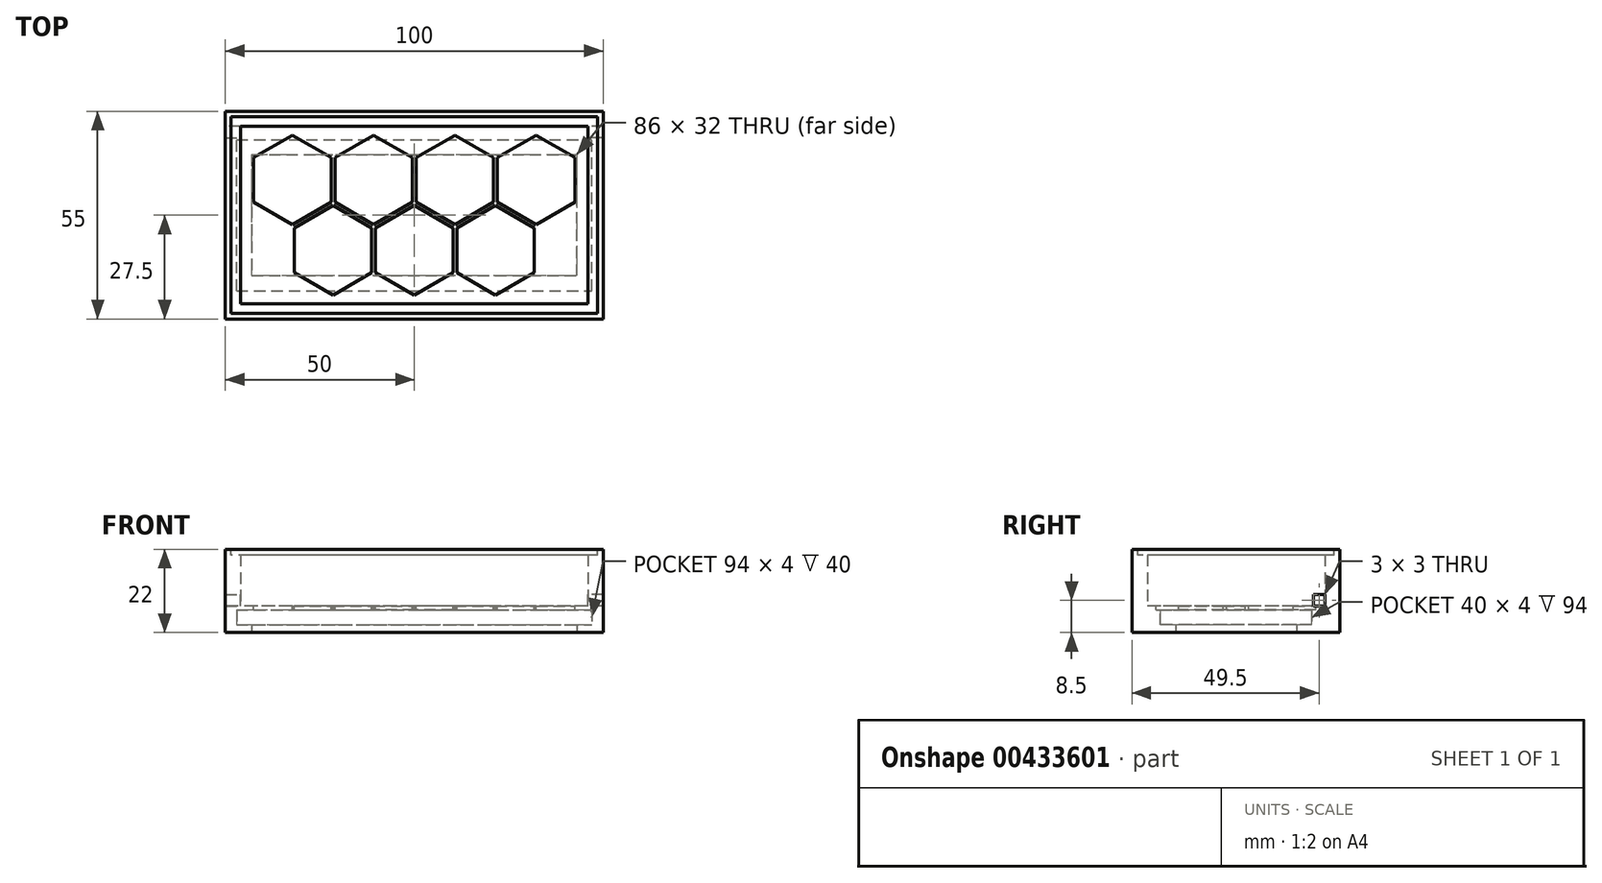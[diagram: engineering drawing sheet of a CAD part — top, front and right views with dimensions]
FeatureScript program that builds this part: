
annotation { "Feature Type Name" : "Feature", "Feature Type Description" : "" }
export const myFeature = defineFeature(function(context is Context, id is Id, definition is map)
    precondition{}
    {
        {
            var Q0;
            Q0=qCreatedBy(makeId("Top.planeOp"),FACE);
            var sketch = newSketch(context, id + "F0", { "sketchPlane" : qUnion([Q0])});
            skLineSegment(sketch, "E0.bottom", {"start": v(50, 27.5) * mm, "end": v(-50, 27.5) * mm});
            skLineSegment(sketch, "E0.top", {"start": v(50, -27.5) * mm, "end": v(-50, -27.5) * mm});
            skLineSegment(sketch, "E0.left", {"start": v(50, 27.5) * mm, "end": v(50, -27.5) * mm});
            skLineSegment(sketch, "E0.right", {"start": v(-50, 27.5) * mm, "end": v(-50, -27.5) * mm});
            skPoint(sketch, "E0.middle", {"position": v(0, 0) * mm});
            skSolve(sketch);
        }
        {
            var Q0;
            Q0=makeQuery(id+"F0.imprint","IMPRINT",FACE,{"disambiguationData":[TD([[makeQuery(id+"F0.imprint","IMPRINT",EDGE,{"derivedFrom":sQuery(id+"F0.wireOp",EDGE,"E0.bottom")}),1.0]])]});
            var Q1;
            Q1=qNothing();
            extrude(context, id + "F1", {"entities" : qUnion([Q0]), "surfaceEntities" : qUnion([Q1]), "depth" : 7 * mm});
        }
        {
            var Q0;
            Q0=makeQuery(id+"F1.opExtrude","CAP_FACE",FACE,{"disambiguationData":[OSD([sQuery(id+"F0.wireOp",EDGE,"E0.bottom"),sQuery(id+"F0.wireOp",EDGE,"E0.top"),sQuery(id+"F0.wireOp",EDGE,"E0.left"),sQuery(id+"F0.wireOp",EDGE,"E0.right")])],"isStart":false});
            var sketch = newSketch(context, id + "F2", { "sketchPlane" : qUnion([Q0])});
            skLineSegment(sketch, "E1.bottom", {"start": v(46, 23.5) * mm, "end": v(-46, 23.5) * mm});
            skLineSegment(sketch, "E1.top", {"start": v(46, -23.5) * mm, "end": v(-46, -23.5) * mm});
            skLineSegment(sketch, "E1.left", {"start": v(46, 23.5) * mm, "end": v(46, -23.5) * mm});
            skLineSegment(sketch, "E1.right", {"start": v(-46, 23.5) * mm, "end": v(-46, -23.5) * mm});
            skPoint(sketch, "E1.middle", {"position": v(0, 0) * mm});
            skSolve(sketch);
        }
        {
            var Q0;
            Q0=makeQuery(id+"F2.imprint","IMPRINT",FACE,{"disambiguationData":[TD([[makeQuery(id+"F2.imprint","IMPRINT",EDGE,{"derivedFrom":sQuery(id+"F2.wireOp",EDGE,"E1.bottom")}),-1.0]])]});
            extrude(context, id + "F3", {"entities" : qUnion([Q0]), "operationType" : NewBodyOperationType.ADD, "depth" : 15 * mm});
        }
        {
            var Q0;
            Q0=makeQuery(id+"F3.opExtrude","CAP_FACE",FACE,{"disambiguationData":[OSD([sQuery(id+"F0.wireOp",EDGE,"E0.bottom"),sQuery(id+"F0.wireOp",EDGE,"E0.top"),sQuery(id+"F0.wireOp",EDGE,"E0.left"),sQuery(id+"F0.wireOp",EDGE,"E0.right"),sQuery(id+"F2.wireOp",EDGE,"E1.bottom"),sQuery(id+"F2.wireOp",EDGE,"E1.top"),sQuery(id+"F2.wireOp",EDGE,"E1.left"),sQuery(id+"F2.wireOp",EDGE,"E1.right")])],"isStart":false});
            var sketch = newSketch(context, id + "F4", { "sketchPlane" : qUnion([Q0])});
            skLineSegment(sketch, "E2.bottom", {"start": v(48.5, 26) * mm, "end": v(-48.5, 26) * mm});
            skLineSegment(sketch, "E2.top", {"start": v(48.5, -26) * mm, "end": v(-48.5, -26) * mm});
            skLineSegment(sketch, "E2.left", {"start": v(48.5, 26) * mm, "end": v(48.5, -26) * mm});
            skLineSegment(sketch, "E2.right", {"start": v(-48.5, 26) * mm, "end": v(-48.5, -26) * mm});
            skSolve(sketch);
        }
        {
            var Q0;
            Q0=makeQuery(id+"F4.imprint","IMPRINT",FACE,{"disambiguationData":[TD([[makeQuery(id+"F4.imprint","IMPRINT",EDGE,{"derivedFrom":sQuery(id+"F4.wireOp",EDGE,"E2.bottom")}),1.0]])]});
            extrude(context, id + "F5", {"entities" : qUnion([Q0]), "operationType" : NewBodyOperationType.REMOVE, "oppositeDirection" : true, "depth" : 1.5 * mm});
        }
        {
            var Q0;
            Q0=makeQuery(id+"F1.opExtrude","CAP_FACE",FACE,{"disambiguationData":[OSD([sQuery(id+"F0.wireOp",EDGE,"E0.bottom"),sQuery(id+"F0.wireOp",EDGE,"E0.top"),sQuery(id+"F0.wireOp",EDGE,"E0.left"),sQuery(id+"F0.wireOp",EDGE,"E0.right")])],"isStart":false});
            var sketch = newSketch(context, id + "F6", { "sketchPlane" : qUnion([Q0])});
            skLineSegment(sketch, "E3", {"start": v(0, -23.5) * mm, "end": v(0, -21.15) * mm});
            skPoint(sketch, "E3.endSnap0", {"position": v(0, -23.5) * mm});
            skCircle(sketch, "E4.cCircle", {"center": v(0, -9.31) * mm, "radius": 11.84 * mm, "construction": true});
            skLineSegment(sketch, "E4.0", {"start": v(0, -21.15) * mm, "end": v(-10.25, -15.23) * mm});
            skLineSegment(sketch, "E4.1", {"start": v(-10.25, -15.23) * mm, "end": v(-10.25, -3.4) * mm});
            skLineSegment(sketch, "E4.2", {"start": v(-10.25, -3.4) * mm, "end": v(0, 2.52) * mm});
            skLineSegment(sketch, "E4.3", {"start": v(0, 2.52) * mm, "end": v(10.25, -3.4) * mm});
            skLineSegment(sketch, "E4.4", {"start": v(10.25, -3.4) * mm, "end": v(10.25, -15.23) * mm});
            skLineSegment(sketch, "E4.5", {"start": v(10.25, -15.23) * mm, "end": v(0, -21.15) * mm});
            skCircle(sketch, "E5.cCircle", {"center": v(-21.5, -9.31) * mm, "radius": 10.25 * mm, "construction": true});
            skLineSegment(sketch, "E5.0", {"start": v(-11.25, -3.4) * mm, "end": v(-11.25, -15.23) * mm});
            skLineSegment(sketch, "E5.1", {"start": v(-11.25, -15.23) * mm, "end": v(-21.5, -21.15) * mm});
            skLineSegment(sketch, "E5.2", {"start": v(-21.5, -21.15) * mm, "end": v(-31.75, -15.23) * mm});
            skLineSegment(sketch, "E5.3", {"start": v(-31.75, -15.23) * mm, "end": v(-31.75, -3.4) * mm});
            skLineSegment(sketch, "E5.4", {"start": v(-31.75, -3.4) * mm, "end": v(-21.5, 2.52) * mm});
            skLineSegment(sketch, "E5.5", {"start": v(-21.5, 2.52) * mm, "end": v(-11.25, -3.4) * mm});
            skPoint(sketch, "E5.0.midPoint", {"position": v(-11.25, -9.31) * mm});
            skCircle(sketch, "E6.cCircle", {"center": v(21.5, -9.31) * mm, "radius": 10.25 * mm, "construction": true});
            skLineSegment(sketch, "E6.0", {"start": v(31.75, -3.4) * mm, "end": v(31.75, -15.23) * mm});
            skLineSegment(sketch, "E6.1", {"start": v(31.75, -15.23) * mm, "end": v(21.5, -21.15) * mm});
            skLineSegment(sketch, "E6.2", {"start": v(21.5, -21.15) * mm, "end": v(11.25, -15.23) * mm});
            skLineSegment(sketch, "E6.3", {"start": v(11.25, -15.23) * mm, "end": v(11.25, -3.4) * mm});
            skLineSegment(sketch, "E6.4", {"start": v(11.25, -3.4) * mm, "end": v(21.5, 2.52) * mm});
            skLineSegment(sketch, "E6.5", {"start": v(21.5, 2.52) * mm, "end": v(31.75, -3.4) * mm});
            skPoint(sketch, "E6.0.midPoint", {"position": v(31.75, -9.31) * mm});
            skCircle(sketch, "E7.cCircle", {"center": v(-32.25, 9.3) * mm, "radius": 10.25 * mm, "construction": true});
            skLineSegment(sketch, "E7.0", {"start": v(-22, 15.23) * mm, "end": v(-22, 3.4) * mm});
            skLineSegment(sketch, "E7.1", {"start": v(-22, 3.4) * mm, "end": v(-32.25, -2.53) * mm});
            skLineSegment(sketch, "E7.2", {"start": v(-32.25, -2.53) * mm, "end": v(-42.5, 3.4) * mm});
            skLineSegment(sketch, "E7.3", {"start": v(-42.5, 3.4) * mm, "end": v(-42.5, 15.23) * mm});
            skLineSegment(sketch, "E7.4", {"start": v(-42.5, 15.23) * mm, "end": v(-32.25, 21.15) * mm});
            skLineSegment(sketch, "E7.5", {"start": v(-32.25, 21.15) * mm, "end": v(-22, 15.23) * mm});
            skPoint(sketch, "E7.0.midPoint", {"position": v(-22, 9.3) * mm});
            skCircle(sketch, "E8.cCircle", {"center": v(-10.75, 9.3) * mm, "radius": 10.25 * mm, "construction": true});
            skLineSegment(sketch, "E8.0", {"start": v(-0.5, 15.23) * mm, "end": v(-0.5, 3.39) * mm});
            skLineSegment(sketch, "E8.1", {"start": v(-0.5, 3.39) * mm, "end": v(-10.75, -2.53) * mm});
            skLineSegment(sketch, "E8.2", {"start": v(-10.75, -2.53) * mm, "end": v(-21, 3.39) * mm});
            skLineSegment(sketch, "E8.3", {"start": v(-21, 3.39) * mm, "end": v(-21, 15.23) * mm});
            skLineSegment(sketch, "E8.4", {"start": v(-21, 15.23) * mm, "end": v(-10.75, 21.15) * mm});
            skLineSegment(sketch, "E8.5", {"start": v(-10.75, 21.15) * mm, "end": v(-0.5, 15.23) * mm});
            skPoint(sketch, "E8.0.midPoint", {"position": v(-0.5, 9.3) * mm});
            skCircle(sketch, "E9.cCircle", {"center": v(10.75, 9.3) * mm, "radius": 10.25 * mm, "construction": true});
            skLineSegment(sketch, "E9.0", {"start": v(21, 15.23) * mm, "end": v(21, 3.39) * mm});
            skLineSegment(sketch, "E9.1", {"start": v(21, 3.39) * mm, "end": v(10.75, -2.53) * mm});
            skLineSegment(sketch, "E9.2", {"start": v(10.75, -2.53) * mm, "end": v(0.5, 3.39) * mm});
            skLineSegment(sketch, "E9.3", {"start": v(0.5, 3.39) * mm, "end": v(0.5, 15.23) * mm});
            skLineSegment(sketch, "E9.4", {"start": v(0.5, 15.23) * mm, "end": v(10.75, 21.14) * mm});
            skLineSegment(sketch, "E9.5", {"start": v(10.75, 21.14) * mm, "end": v(21, 15.23) * mm});
            skPoint(sketch, "E9.0.midPoint", {"position": v(21, 9.3) * mm});
            skCircle(sketch, "E10.cCircle", {"center": v(32.25, 9.3) * mm, "radius": 10.25 * mm, "construction": true});
            skLineSegment(sketch, "E10.0", {"start": v(42.5, 15.23) * mm, "end": v(42.5, 3.39) * mm});
            skLineSegment(sketch, "E10.1", {"start": v(42.5, 3.39) * mm, "end": v(32.25, -2.53) * mm});
            skLineSegment(sketch, "E10.2", {"start": v(32.25, -2.53) * mm, "end": v(22, 3.39) * mm});
            skLineSegment(sketch, "E10.3", {"start": v(22, 3.39) * mm, "end": v(22, 15.23) * mm});
            skLineSegment(sketch, "E10.4", {"start": v(22, 15.23) * mm, "end": v(32.25, 21.14) * mm});
            skLineSegment(sketch, "E10.5", {"start": v(32.25, 21.14) * mm, "end": v(42.5, 15.23) * mm});
            skPoint(sketch, "E10.0.midPoint", {"position": v(42.5, 9.3) * mm});
            skSolve(sketch);
        }
        {
            var Q0;
            Q0=makeQuery(id+"F3.opExtrude","SWEPT_FACE",FACE,{"disambiguationData":[OSD([sQuery(id+"F2.wireOp",EDGE,"E1.left")])]});
            var sketch = newSketch(context, id + "F7", { "sketchPlane" : qUnion([Q0])});
            skLineSegment(sketch, "E11.bottom", {"start": v(-23.5, 7) * mm, "end": v(-20.5, 7) * mm});
            skLineSegment(sketch, "E11.top", {"start": v(-23.5, 10) * mm, "end": v(-20.5, 10) * mm});
            skLineSegment(sketch, "E11.left", {"start": v(-23.5, 7) * mm, "end": v(-23.5, 10) * mm});
            skLineSegment(sketch, "E11.right", {"start": v(-20.5, 7) * mm, "end": v(-20.5, 10) * mm});
            skSolve(sketch);
        }
        {
            var Q0;
            Q0=makeQuery(id+"F7.imprint","IMPRINT",FACE,{"disambiguationData":[TD([[makeQuery(id+"F7.imprint","IMPRINT",EDGE,{"derivedFrom":sQuery(id+"F7.wireOp",EDGE,"E11.bottom")}),1.0]])]});
            extrude(context, id + "F8", {"entities" : qUnion([Q0]), "operationType" : NewBodyOperationType.REMOVE, "oppositeDirection" : true, "depth" : 5 * mm});
        }
        {
            var Q0;
            Q0=makeQuery(id+"F3.opExtrude","SWEPT_FACE",FACE,{"disambiguationData":[OSD([sQuery(id+"F2.wireOp",EDGE,"E1.right")])]});
            var sketch = newSketch(context, id + "F9", { "sketchPlane" : qUnion([Q0])});
            skLineSegment(sketch, "E12.bottom", {"start": v(23.5, 7) * mm, "end": v(20.5, 7) * mm});
            skLineSegment(sketch, "E12.top", {"start": v(23.5, 10) * mm, "end": v(20.5, 10) * mm});
            skLineSegment(sketch, "E12.left", {"start": v(23.5, 7) * mm, "end": v(23.5, 10) * mm});
            skLineSegment(sketch, "E12.right", {"start": v(20.5, 7) * mm, "end": v(20.5, 10) * mm});
            skSolve(sketch);
        }
        {
            var Q0;
            Q0=makeQuery(id+"F9.imprint","IMPRINT",FACE,{"disambiguationData":[TD([[makeQuery(id+"F9.imprint","IMPRINT",EDGE,{"derivedFrom":sQuery(id+"F9.wireOp",EDGE,"E12.bottom")}),-1.0]])]});
            extrude(context, id + "F10", {"entities" : qUnion([Q0]), "operationType" : NewBodyOperationType.REMOVE, "oppositeDirection" : true, "depth" : 5 * mm});
        }
        {
            var Q0;
            {var subQ0=sQuery(id+"F0.wireOp",EDGE,"E0.left");Q0=makeQuery(id+"F3.boolean.opBoolean","MERGE",FACE,{"derivedFrom":[makeQuery(id+"F1.opExtrude","SWEPT_FACE",FACE,{"disambiguationData":[OSD([subQ0])]}),makeQuery(id+"F3.opExtrude","SWEPT_FACE",FACE,{"disambiguationData":[OSD([subQ0])]})]});}
            var sketch = newSketch(context, id + "F11", { "sketchPlane" : qUnion([Q0])});
            skLineSegment(sketch, "E13", {"start": v(-20, 0) * mm, "end": v(-20, 6) * mm});
            skLineSegment(sketch, "E14", {"start": v(-20, 6) * mm, "end": v(20, 6) * mm});
            skLineSegment(sketch, "E15", {"start": v(20, 6) * mm, "end": v(20, 0) * mm});
            skSolve(sketch);
        }
        {
            var Q0;
            {var subQ0=sQuery(id+"F11.wireOp",EDGE,"E13");Q0=makeQuery(id+"F11.imprint","IMPRINT",FACE,{"disambiguationData":[TD([[makeQuery(id+"F11.imprint","IMPRINT",EDGE,{"derivedFrom":subQ0}),-1.0]])]});}
            extrude(context, id + "F12", {"entities" : qUnion([Q0]), "operationType" : NewBodyOperationType.REMOVE, "oppositeDirection" : true, "depth" : 100 * mm});
        }
        {
            var Q0;
            {var subQ0=sQuery(id+"F0.wireOp",EDGE,"E0.left");Q0=makeQuery(id+"F3.boolean.opBoolean","MERGE",FACE,{"derivedFrom":[makeQuery(id+"F1.opExtrude","SWEPT_FACE",FACE,{"disambiguationData":[OSD([subQ0])]}),makeQuery(id+"F3.opExtrude","SWEPT_FACE",FACE,{"disambiguationData":[OSD([subQ0])]})]});}
            var sketch = newSketch(context, id + "F13", { "sketchPlane" : qUnion([Q0])});
            skLineSegment(sketch, "E16", {"start": v(-16, 2) * mm, "end": v(-20, 2) * mm});
            skLineSegment(sketch, "E17", {"start": v(16, 2) * mm, "end": v(20, 2) * mm});
            skLineSegment(sketch, "E18", {"start": v(16, 2) * mm, "end": v(16, 0) * mm});
            skLineSegment(sketch, "E19", {"start": v(16, 0) * mm, "end": v(20, 0) * mm});
            skLineSegment(sketch, "E20", {"start": v(-16, 2) * mm, "end": v(-16, 0) * mm});
            skLineSegment(sketch, "E21", {"start": v(-16, 0) * mm, "end": v(-20, 0) * mm});
            skSolve(sketch);
        }
        {
            var Q0;
            {var subQ0=sQuery(id+"F13.wireOp",EDGE,"E17");Q0=makeQuery(id+"F13.imprint","IMPRINT",FACE,{"disambiguationData":[TD([[makeQuery(id+"F13.imprint","IMPRINT",EDGE,{"derivedFrom":subQ0}),-1.0]])]});}
            var Q1;
            {var subQ0=sQuery(id+"F13.wireOp",EDGE,"E16");Q1=makeQuery(id+"F13.imprint","IMPRINT",FACE,{"disambiguationData":[TD([[makeQuery(id+"F13.imprint","IMPRINT",EDGE,{"derivedFrom":subQ0}),1.0]])]});}
            extrude(context, id + "F14", {"entities" : qUnion([Q0, Q1]), "operationType" : NewBodyOperationType.ADD, "oppositeDirection" : true, "depth" : 100 * mm});
        }
        {
            var Q0;
            {var subQ0=sQuery(id+"F0.wireOp",EDGE,"E0.left");Q0=makeQuery(id+"F14.boolean.opBoolean","MERGE",FACE,{"derivedFrom":[makeQuery(id+"F3.boolean.opBoolean","MERGE",FACE,{"derivedFrom":[makeQuery(id+"F1.opExtrude","SWEPT_FACE",FACE,{"disambiguationData":[OSD([subQ0])]}),makeQuery(id+"F3.opExtrude","SWEPT_FACE",FACE,{"disambiguationData":[OSD([subQ0])]})]}),makeQuery(id+"F14.opExtrude","CAP_FACE",FACE,{"disambiguationData":[OSD([sQuery(id+"F11.wireOp",EDGE,"E13"),sQuery(id+"F13.wireOp",EDGE,"E16"),sQuery(id+"F13.wireOp",EDGE,"E20"),sQuery(id+"F13.wireOp",EDGE,"E21")])],"isStart":true}),makeQuery(id+"F14.opExtrude","CAP_FACE",FACE,{"disambiguationData":[OSD([sQuery(id+"F11.wireOp",EDGE,"E15"),sQuery(id+"F13.wireOp",EDGE,"E17"),sQuery(id+"F13.wireOp",EDGE,"E18"),sQuery(id+"F13.wireOp",EDGE,"E19")])],"isStart":true})]});}
            var sketch = newSketch(context, id + "F15", { "sketchPlane" : qUnion([Q0])});
            skLineSegment(sketch, "E22", {"start": v(-16, 0) * mm, "end": v(16, 0) * mm});
            skSolve(sketch);
        }
        {
            var Q0;
            Q0=makeQuery(id+"F15.imprint","IMPRINT",FACE,{"disambiguationData":[TD([[makeQuery(id+"F15.imprint","IMPRINT",EDGE,{"derivedFrom":sQuery(id+"F15.wireOp",EDGE,"E22")}),1.0]])]});
            extrude(context, id + "F16", {"entities" : qUnion([Q0]), "operationType" : NewBodyOperationType.ADD, "oppositeDirection" : true, "depth" : 7 * mm});
        }
        {
            var Q0;
            {var subQ0=sQuery(id+"F0.wireOp",EDGE,"E0.right");Q0=makeQuery(id+"F14.boolean.opBoolean","MERGE",FACE,{"derivedFrom":[makeQuery(id+"F3.boolean.opBoolean","MERGE",FACE,{"derivedFrom":[makeQuery(id+"F1.opExtrude","SWEPT_FACE",FACE,{"disambiguationData":[OSD([subQ0])]}),makeQuery(id+"F3.opExtrude","SWEPT_FACE",FACE,{"disambiguationData":[OSD([subQ0])]})]}),makeQuery(id+"F14.opExtrude","CAP_FACE",FACE,{"disambiguationData":[OSD([sQuery(id+"F11.wireOp",EDGE,"E13"),sQuery(id+"F13.wireOp",EDGE,"E16"),sQuery(id+"F13.wireOp",EDGE,"E20"),sQuery(id+"F13.wireOp",EDGE,"E21")])],"isStart":false}),makeQuery(id+"F14.opExtrude","CAP_FACE",FACE,{"disambiguationData":[OSD([sQuery(id+"F11.wireOp",EDGE,"E15"),sQuery(id+"F13.wireOp",EDGE,"E17"),sQuery(id+"F13.wireOp",EDGE,"E18"),sQuery(id+"F13.wireOp",EDGE,"E19")])],"isStart":false})]});}
            var sketch = newSketch(context, id + "F17", { "sketchPlane" : qUnion([Q0])});
            skLineSegment(sketch, "E23", {"start": v(-16, 0) * mm, "end": v(16, 0) * mm});
            skSolve(sketch);
        }
        {
            var Q0;
            Q0=makeQuery(id+"F17.imprint","IMPRINT",FACE,{"disambiguationData":[TD([[makeQuery(id+"F17.imprint","IMPRINT",EDGE,{"derivedFrom":sQuery(id+"F17.wireOp",EDGE,"E23")}),1.0]])]});
            extrude(context, id + "F18", {"entities" : qUnion([Q0]), "operationType" : NewBodyOperationType.ADD, "oppositeDirection" : true, "depth" : 7 * mm});
        }
        {
            var Q0;
            Q0=makeQuery(id+"F16.opExtrude","CAP_FACE",FACE,{"disambiguationData":[OSD([sQuery(id+"F11.wireOp",EDGE,"E13"),sQuery(id+"F11.wireOp",EDGE,"E14"),sQuery(id+"F11.wireOp",EDGE,"E15"),sQuery(id+"F13.wireOp",EDGE,"E16"),sQuery(id+"F13.wireOp",EDGE,"E17"),sQuery(id+"F13.wireOp",EDGE,"E18"),sQuery(id+"F13.wireOp",EDGE,"E20"),sQuery(id+"F15.wireOp",EDGE,"E22")])],"isStart":false});
            var sketch = newSketch(context, id + "F19", { "sketchPlane" : qUnion([Q0])});
            skLineSegment(sketch, "E24", {"start": v(16, 2) * mm, "end": v(-16, 2) * mm});
            skSolve(sketch);
        }
        {
            var Q0;
            Q0 = qSketchRegion(id + "F19", true);
            var Q1;
            Q1=makeQuery(id+"F19.imprint","IMPRINT",FACE,{"disambiguationData":[TD([[makeQuery(id+"F19.imprint","IMPRINT",EDGE,{"derivedFrom":sQuery(id+"F19.wireOp",EDGE,"E24")}),-1.0]])]});
            extrude(context, id + "F20", {"entities" : qUnion([Q0, Q1]), "operationType" : NewBodyOperationType.REMOVE, "oppositeDirection" : true, "depth" : 4 * mm});
        }
        {
            var Q0;
            Q0=makeQuery(id+"F18.opExtrude","CAP_FACE",FACE,{"disambiguationData":[OSD([sQuery(id+"F11.wireOp",EDGE,"E13"),sQuery(id+"F11.wireOp",EDGE,"E14"),sQuery(id+"F11.wireOp",EDGE,"E15"),sQuery(id+"F13.wireOp",EDGE,"E16"),sQuery(id+"F13.wireOp",EDGE,"E17"),sQuery(id+"F13.wireOp",EDGE,"E18"),sQuery(id+"F13.wireOp",EDGE,"E20"),sQuery(id+"F17.wireOp",EDGE,"E23")])],"isStart":false});
            var sketch = newSketch(context, id + "F21", { "sketchPlane" : qUnion([Q0])});
            skLineSegment(sketch, "E25", {"start": v(-16, 2) * mm, "end": v(16, 2) * mm});
            skSolve(sketch);
        }
        {
            var Q0;
            Q0=makeQuery(id+"F21.imprint","IMPRINT",FACE,{"disambiguationData":[TD([[makeQuery(id+"F21.imprint","IMPRINT",EDGE,{"derivedFrom":sQuery(id+"F21.wireOp",EDGE,"E25")}),1.0]])]});
            extrude(context, id + "F22", {"entities" : qUnion([Q0]), "operationType" : NewBodyOperationType.REMOVE, "oppositeDirection" : true, "depth" : 4 * mm});
        }
        {
            var Q0;
            Q0=makeQuery(id+"F6.imprint","IMPRINT",FACE,{"disambiguationData":[TD([[makeQuery(id+"F6.imprint","IMPRINT",EDGE,{"derivedFrom":sQuery(id+"F6.wireOp",EDGE,"E7.0")}),-1.0]])]});
            var Q1;
            Q1=makeQuery(id+"F6.imprint","IMPRINT",FACE,{"disambiguationData":[TD([[makeQuery(id+"F6.imprint","IMPRINT",EDGE,{"derivedFrom":sQuery(id+"F6.wireOp",EDGE,"E8.0")}),-1.0]])]});
            var Q2;
            Q2=makeQuery(id+"F6.imprint","IMPRINT",FACE,{"disambiguationData":[TD([[makeQuery(id+"F6.imprint","IMPRINT",EDGE,{"derivedFrom":sQuery(id+"F6.wireOp",EDGE,"E9.0")}),-1.0]])]});
            var Q3;
            Q3=makeQuery(id+"F6.imprint","IMPRINT",FACE,{"disambiguationData":[TD([[makeQuery(id+"F6.imprint","IMPRINT",EDGE,{"derivedFrom":sQuery(id+"F6.wireOp",EDGE,"E10.0")}),-1.0]])]});
            var Q4;
            Q4=makeQuery(id+"F6.imprint","IMPRINT",FACE,{"disambiguationData":[TD([[makeQuery(id+"F6.imprint","IMPRINT",EDGE,{"derivedFrom":sQuery(id+"F6.wireOp",EDGE,"E6.0")}),-1.0]])]});
            var Q5;
            Q5=makeQuery(id+"F6.imprint","IMPRINT",FACE,{"disambiguationData":[TD([[makeQuery(id+"F6.imprint","IMPRINT",EDGE,{"derivedFrom":sQuery(id+"F6.wireOp",EDGE,"E4.0")}),-1.0]])]});
            var Q6;
            Q6=makeQuery(id+"F6.imprint","IMPRINT",FACE,{"disambiguationData":[TD([[makeQuery(id+"F6.imprint","IMPRINT",EDGE,{"derivedFrom":sQuery(id+"F6.wireOp",EDGE,"E5.0")}),-1.0]])]});
            extrude(context, id + "F23", {"entities" : qUnion([Q0, Q1, Q2, Q3, Q4, Q5, Q6]), "operationType" : NewBodyOperationType.REMOVE, "oppositeDirection" : true, "depth" : .95 * mm});
        }
    });
